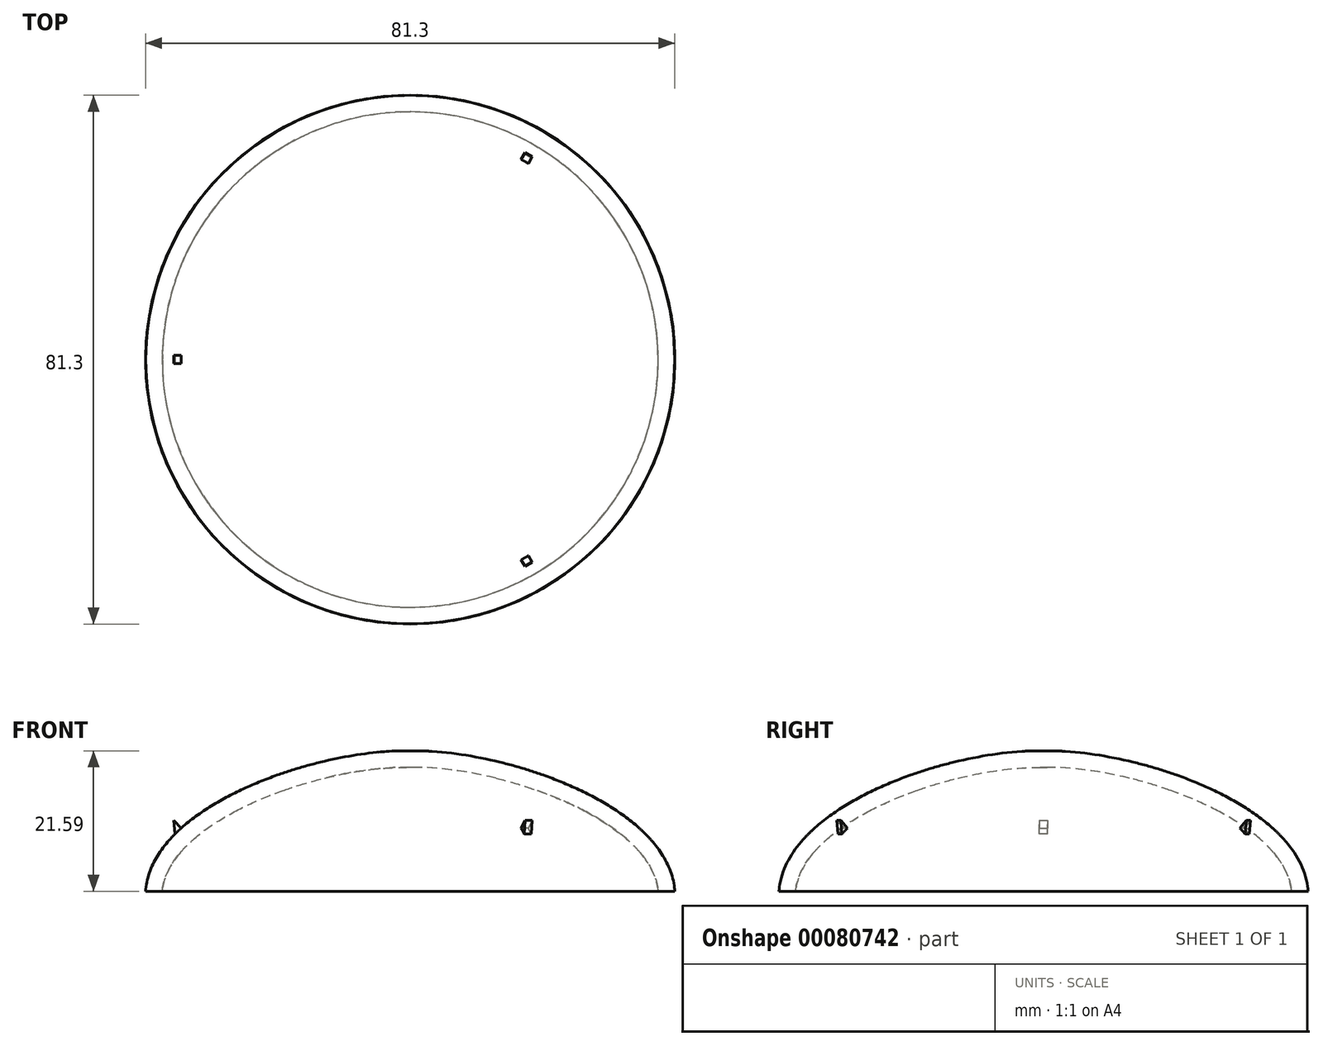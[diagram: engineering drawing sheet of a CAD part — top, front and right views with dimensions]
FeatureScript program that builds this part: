
annotation { "Feature Type Name" : "Feature", "Feature Type Description" : "" }
export const myFeature = defineFeature(function(context is Context, id is Id, definition is map)
    precondition{}
    {
        {
            var Q0;
            Q0=qCreatedBy(makeId("Front.planeOp"),FACE);
            var sketch = newSketch(context, id + "F0", { "sketchPlane" : qUnion([Q0])});
            skFitSpline(sketch, "E0", {"points": [v(0, 19.05) * mm, v(-38.1, 0) * mm], "startDerivative": vector(-42.58, 0.67) * mm, "endDerivative": vector(-3.13, -32.75) * mm});
            skLineSegment(sketch, "E1", {"start": v(0, 19.05) * mm, "end": v(0, 0) * mm});
            skLineSegment(sketch, "E2", {"start": v(0, 0) * mm, "end": v(-38.1, 0) * mm});
            skLineSegment(sketch, "E3", {"start": v(-19.58, 15.46) * mm, "end": v(-22.27, 18.92) * mm});
            skLineSegment(sketch, "E4", {"start": v(-22.27, 18.92) * mm, "end": v(-23.75, 16.09) * mm});
            skLineSegment(sketch, "E5", {"start": v(-23.75, 16.09) * mm, "end": v(-23.04, 14.12) * mm});
            skLineSegment(sketch, "E6", {"start": v(-35.32, 5.94) * mm, "end": v(-36.09, 8.32) * mm});
            skLineSegment(sketch, "E7", {"start": v(-36.09, 8.32) * mm, "end": v(-36.36, 10.92) * mm});
            skLineSegment(sketch, "E8", {"start": v(-36.36, 10.92) * mm, "end": v(-33.43, 7.86) * mm});
            skLineSegment(sketch, "E9", {"start": v(-29.75, 10.62) * mm, "end": v(-31.05, 12.74) * mm});
            skLineSegment(sketch, "E10", {"start": v(-31.05, 12.74) * mm, "end": v(-31.05, 14.75) * mm});
            skLineSegment(sketch, "E11", {"start": v(-31.05, 14.75) * mm, "end": v(-28.65, 13.74) * mm});
            skLineSegment(sketch, "E12", {"start": v(-28.65, 13.74) * mm, "end": v(-27.04, 12.2) * mm});
            skLineSegment(sketch, "E13", {"start": v(-13.17, 17.38) * mm, "end": v(-14.8, 18.9) * mm});
            skLineSegment(sketch, "E14", {"start": v(-14.8, 18.9) * mm, "end": v(-14.7, 21.08) * mm});
            skLineSegment(sketch, "E15", {"start": v(-14.7, 21.08) * mm, "end": v(-11.43, 20.07) * mm});
            skLineSegment(sketch, "E16", {"start": v(-11.43, 20.07) * mm, "end": v(-10.7, 17.94) * mm});
            skSolve(sketch);
        }
        {
            var Q0;
            Q0=makeQuery(id+"F0.imprint","IMPRINT",FACE,{"disambiguationData":[TD([[makeQuery(id+"F0.imprint","IMPRINT",EDGE,{"derivedFrom":sQuery(id+"F0.wireOp",EDGE,"E0")}),1.0]])]});
            var Q1;
            Q1=sQuery(id+"F0.wireOp",EDGE,"E1");
            revolve(context, id + "F1", {"entities" : qUnion([Q0]), "axis" : qUnion([Q1]), "revolveType" : RevolveType.FULL});
        }
        {
            var Q0;
            Q0=makeQuery(id+"F1.opRevolve","SWEPT_FACE",FACE,{"disambiguationData":[OSD([sQuery(id+"F0.wireOp",EDGE,"E2")])]});
            shell(context, id + "F2", {"entities" : qUnion([Q0]), "thickness" : 2.54 * mm, "oppositeDirection" : true});
        }
        {
            var Q0;
            {var subQ0=sQuery(id+"F0.wireOp",EDGE,"E3");Q0=makeQuery(id+"F0.imprint","IMPRINT",FACE,{"disambiguationData":[TD([[makeQuery(id+"F0.imprint","IMPRINT",EDGE,{"derivedFrom":subQ0}),1.0]])]});}
            var Q1;
            {var subQ0=sQuery(id+"F0.wireOp",EDGE,"E6");Q1=makeQuery(id+"F0.imprint","IMPRINT",FACE,{"disambiguationData":[TD([[makeQuery(id+"F0.imprint","IMPRINT",EDGE,{"derivedFrom":subQ0}),-1.0]])]});}
            var Q2;
            {var subQ0=sQuery(id+"F0.wireOp",EDGE,"E9");Q2=makeQuery(id+"F0.imprint","IMPRINT",FACE,{"disambiguationData":[TD([[makeQuery(id+"F0.imprint","IMPRINT",EDGE,{"derivedFrom":subQ0}),-1.0]])]});}
            var Q3;
            {var subQ0=sQuery(id+"F0.wireOp",EDGE,"E13");Q3=makeQuery(id+"F0.imprint","IMPRINT",FACE,{"disambiguationData":[TD([[makeQuery(id+"F0.imprint","IMPRINT",EDGE,{"derivedFrom":subQ0}),-1.0]])]});}
            extrude(context, id + "F3", {"entities" : qUnion([Q0, Q1, Q2, Q3]), "operationType" : NewBodyOperationType.ADD, "endBound" : BoundingType.SYMMETRIC, "depth" : 1.27 * mm});
        }
        {
            var Q0;
            Q0=makeQuery(id+"F1.opRevolve","SWEPT_BODY",BODY,{"disambiguationData":[OSD([sQuery(id+"F0.wireOp",EDGE,"E0"),sQuery(id+"F0.wireOp",EDGE,"E1"),sQuery(id+"F0.wireOp",EDGE,"E2")])]});
            var Q1;
            Q1=makeQuery(id+"F2.opShell","OFFSET_EDGE",EDGE,{"disambiguationData":[OSD([sQuery(id+"F0.wireOp",EDGE,"E0"),sQuery(id+"F0.wireOp",EDGE,"E2")])]});
            circularPattern(context, id + "F4", {"entities" : qUnion([Q0]), "axis" : qUnion([Q1]), "angle" : 360 * degree, "instanceCount" : 3, "equalSpace" : true});
        }
    });
